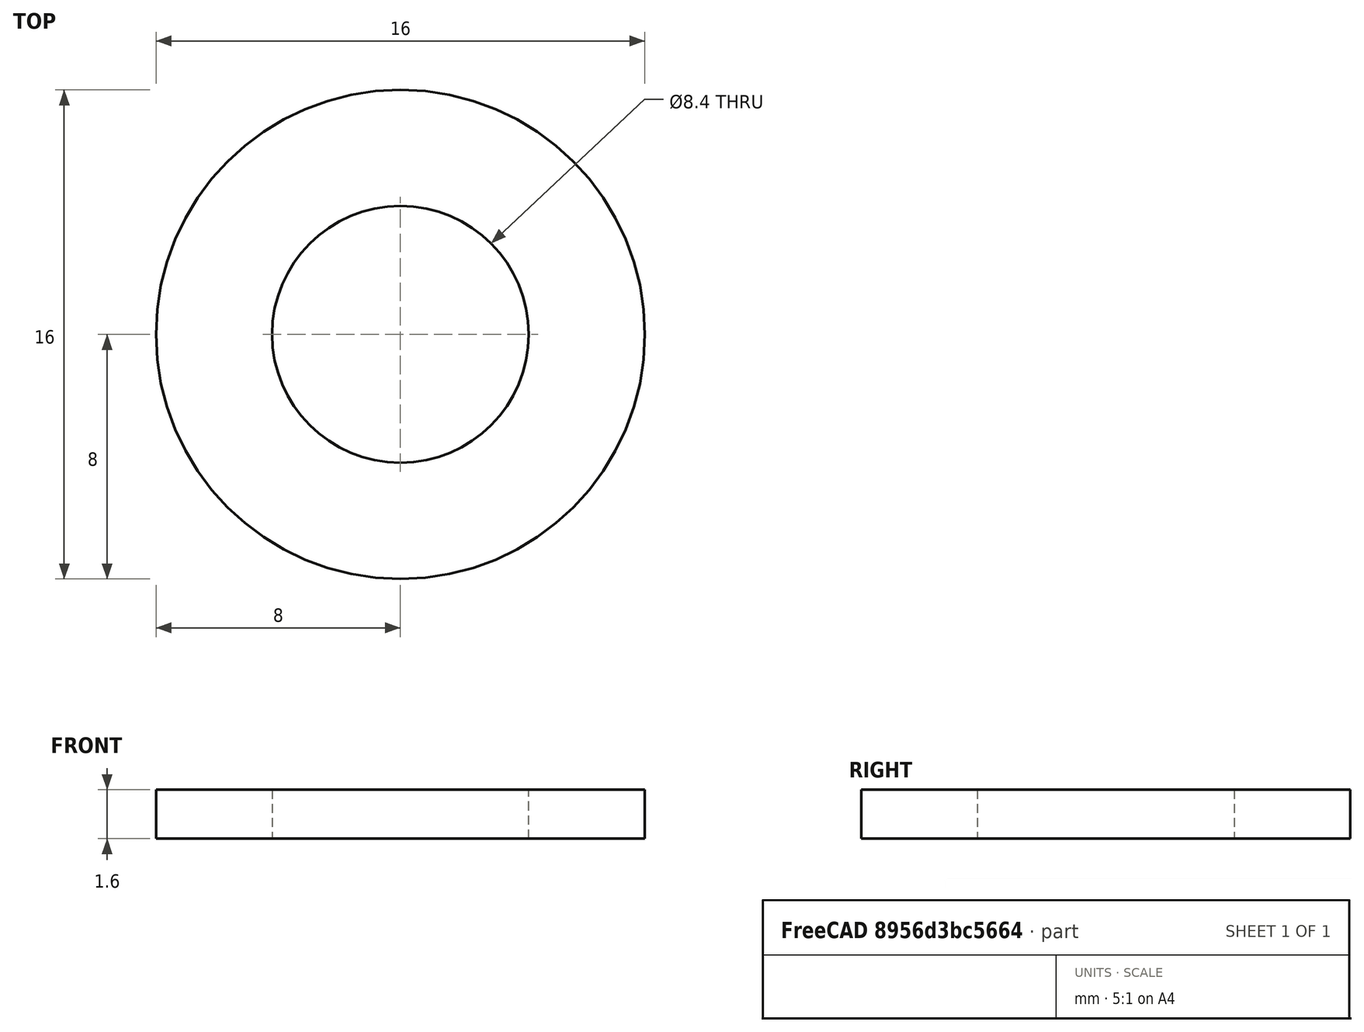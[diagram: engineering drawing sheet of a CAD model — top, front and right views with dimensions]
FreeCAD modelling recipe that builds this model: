
FCSTD DOCUMENT  (FreeCAD 0.18R16110 (Git))
Label: m8washer
License: All rights reserved
LicenseURL: http://en.wikipedia.org/wiki/All_rights_reserved
objects: Sketcher::SketchObject×1, PartDesign::Pad×1, PartDesign::Body×1
note: 4 computed .brp shape members not serialized (recipe doc carries the construction recipe); baked Part::Feature solids carry a one-line shape summary decoded from their .brp

FEATURE [Sketcher::SketchObject] Sketch
  MapMode = 5
  Support = -> [XY_Plane]
  sketch-geometry (2):
    g0: Circle CenterX=0 CenterY=0 CenterZ=0 NormalX=0 NormalY=0 NormalZ=1 AngleXU=0 Radius=8
    g1: Circle CenterX=0 CenterY=0 CenterZ=0 NormalX=0 NormalY=0 NormalZ=1 AngleXU=0 Radius=4.2
  constraints (4):
    c: Radius(g0) = 8
    c: Radius(g1) = 4.2
    c: Coincident(g1,g-1)
    c: Coincident(g0,g1)
FEATURE [PartDesign::Pad] Pad
  Length = 1.6
  Length2 = 100
  Profile = -> Sketch
  Type = 0
FEATURE [PartDesign::Body] Body  label="M8washer"
  Group = -> [Sketch,Pad]
  Origin = -> Origin
  Tip = -> Pad
